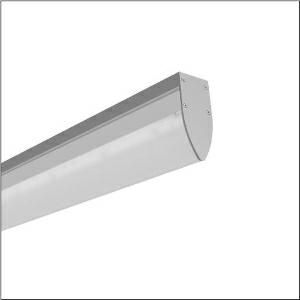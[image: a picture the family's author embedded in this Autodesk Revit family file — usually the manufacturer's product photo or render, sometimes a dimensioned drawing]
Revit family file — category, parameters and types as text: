
# Revit family: mira_r__21_td_51fr527k474a_9fa0
name_source: partatom
category: Lighting Fixtures
units: mm (PartAtom-declared; Revit-internal decimal feet)

## family parameters
Cut with Voids When Loaded = No
Host = Face
Light Source = No
Part Type = Normal
Room Calculation Point = No
Round Connector Dimension = Use Diameter
Shared = No

## types (1)
- Mira® 21 TD (1 x LED, 7330 lm, 52 W, 4000K)
    Apparent Load = 52 VA
    CIE Flux Codes = 40 68 87 81 100
    Color Rendering = 80
    Color Temperature = 4000K
    Default Elevation = 1800 mm
    Description = Mira® 21 TD, clean room luminaire, primary light control with reflector, primary optical cover: cover, of PMMA, frosted, light emission: direct distribution, primary light characteristic: symmetric, installation type: surface-mounted, LED, rated luminous flux: 7.330lm, luminous efficacy: 141lm/W, light colour: 840, colour temperature: 4000K, control gear: ON/OFF, with terminal, 3-pole, max. 2.5mm², mains connection: 230V, AC, 50/60Hz, rated input power: 52W, luminaire housing, of sheet steel, coated, pure white (RAL 9010), length: 1.200mm, width: 55mm, height: 120mm, protection rating (complete): IP43, insulation class (complete): insulation class I (protective earthing), certification: CE, UKCA, permissible operating ambient temperature: -5..+40°C, standard: EN 50419, packaging unit: 1 piece
    Height = 120 mm
    Lamp = 1 x LED
    Lamp Light Flux = 7330 lm
    Lamp Power = 52 W
    Lamp count = 1
    Length = 1200 mm
    Luminous efficacy = 141 lm/W
    Manufacturer = Siteco
    ModVariant = No
    Model = 51FR527K474A
    Mounting Place = Ceiling
    Mounting Type = Surface mounted
    Number of Poles = 1
    OnlyDefault = Yes
    Power Factor = 1
    Product Name = Mira® 21 TD
    Product group = clean room luminaire | ceiling mounted
    ProductGroupID = 305
    Protection Class = Protection class I
    Protection Degree = IP 43
    RLX_Detail_Level = 1
    RLX_Emergency_Light_Flux = 0 lm
    RLX_Emergency_Type = 0
    RLX_Emergency_Type_DB = No
    RlxData = <blob elided: 25141 chars, md5=03b69573>
    Socket = socket
    Standby Power = 0 W
    System Light Flux = 7330 lm
    System Power = 52 W
    Type Comments = Product without accessories
    Type Image = l_1007115.jpg
    URL = http://relux.com
    VarID = ---
    Voltage = 0 V
    Weight = 0.00 kg
    Width = 55 mm

## geometry (parser evidence)
native form markers: Blend x4, Sweep x11
no freeform markers — native parametric forms only
